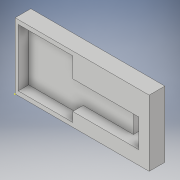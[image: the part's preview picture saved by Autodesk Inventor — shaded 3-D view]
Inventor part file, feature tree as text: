
AUTODESK INVENTOR PART (.ipt)
format: ipt  version: 2017 (Build 210142000, 142)  size: 153,600 bytes
history: native  units: in
note: dims shown in document units (in); Inventor stores cm internally (conversion verified against a paired STEP export)
features: extrude x7, sketch x7
ambient origin geometry x8: Origin, YZ Plane, XZ Plane, XY Plane, X Axis, Y Axis, Z Axis, Center Point
bodies: Solid1 (feature_tree)
feature tree (14):
  extrude  "Extrusion1"  Depth=2.1654in
  extrude  "Extrusion3"  Depth=0.1969in
  extrude  "Extrusion4"  Depth=0.3543in
  extrude  "Extrusion5"  Depth=1.063in
  extrude  "Extrusion6"  Depth=0.5906in
  extrude  "Extrusion7"  Depth=2.4803in
  extrude  "Extrusion8"  TaperAngle=90.0deg  [1 undecoded]
  sketch  "Sketch17"  dims[d36=5.0394in d37=90.0deg d38=0.3937in d39=0.0in d40=0.1969in d41=0.0in d42=0.0787in d43=0.3937in d44=0.0in d45=0.0787in d46=0.3937in d47=0.0in]
  sketch  "Sketch7"  dims[d0=4.9213in d1=2.1654in]
  sketch  "Sketch8"  dims[d2=0.1969in d3=0.0in d20=2.9528in]
  sketch  "Sketch9"  dims[d21=0.3937in d22=0.0in d23=0.3543in]
  sketch  "Sketch12"  dims[d24=2.5591in d25=1.063in]
  sketch  "Sketch14"  dims[d26=0.3937in d27=0.0in d28=0.5906in]
  sketch  "Sketch15"  dims[d29=0.7874in d30=0.0in d35=2.4803in]
note: 1 required parameter value undecoded (feature->parameter linkage not recoverable at this tier; creation-order binding heuristic only, values carry confidence <= 0.55)
